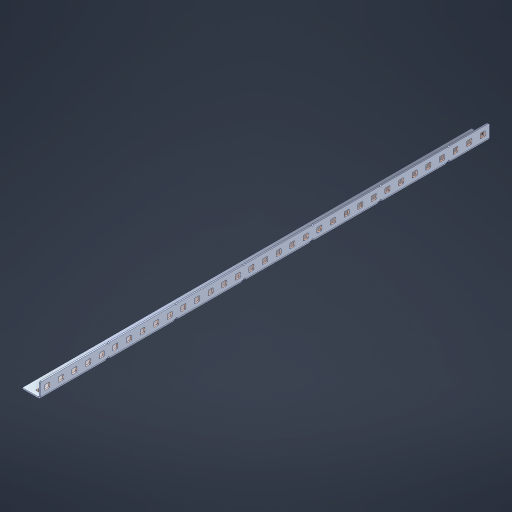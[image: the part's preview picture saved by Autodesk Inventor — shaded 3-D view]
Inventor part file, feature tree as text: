
AUTODESK INVENTOR PART (.ipt)
format: ipt  version: 2023 (Build 270158000, 158)  size: 1,009,152 bytes
history: native  units: in
note: dims shown in document units (in); Inventor stores cm internally (conversion verified against a paired STEP export)
features: other x71, extrude x65, sheet_metal_op x10, sketch x8, mirror x1, pattern_linear x1, chamfer x1
ambient origin geometry x8: Origin, YZ Plane, XZ Plane, XY Plane, X Axis, Y Axis, Z Axis, Center Point
bodies: Solid1 (feature_tree), Body (feature_tree)
feature tree (157):
  other  "Flange Pattern Plane"
  sheet_metal_op  "Flange Pattern"
  sheet_metal_op  "Body Pattern"
  other  "Arc Length"
  mirror  "Notch Mirror"
  pattern_linear  "Notch Pattern"  Spacing1=0.1875in  [1 undecoded]
  chamfer  "End Chamfer"
  extrude  "Half Cut"  Depth=0.0469in
  sketch  "Sketch1"  dims[d0=2.5in]
  other  "Plate1"
  sketch  "Sketch2"  dims[d1=16.5in]
  other  "Plate2"
  sheet_metal_op  "Bend1"
  sheet_metal_op  "Corner1"
  sketch  "Sketch3"  dims[d2=0.0469in]
  other  "Flange Pattern Sketch"
  sketch  "Sketch7"  dims[d3=0.0469in]
  other  "Srf1"
  other  "Srf2"
  sketch  "Sketch8"  dims[d4=0.0234in]
  sketch  "Sketch9"  dims[d5=0.0938in]
  other  "Srf91"
  sheet_metal_op  "Body Pattern Sketch"
  other  "Srf92"
  sketch  "Sketch13"  dims[d6=0.0469in]
  sketch  "Sketch14"  dims[d7=0.5in d8=90.0deg d9=0.0312in d10=0.1875in d11=0.0469in d12=0.0469in d16=0.182in d17=0.02in d18=0.0469in d19=0.0in d20=0.25in d21=0.25in d46=0.172in d47=1.0in d48=0.0in d49=0.182in d50=0.02in d51=0.25in d52=0.25in d53=0.0469in d54=0.0in d55=0.172in d56=1.0in d57=0.0in d60=12.9921in d62=0.5in d63=0.3937in d65=0.5in d85=0.1227in d86=0.1659in d88=0.04in d89=0.0469in d90=0.0in d91=0.04in d92=0.0491in d95=2.5in d96=0.04in d97=0.25in d98=45.0deg d101=0.0in d102=2.497in d131=0.5in d132=12.9921in d134=0.5in d139=0.5in]
  other  "Srf856"
  other  "Srf1310"
  other  "Srf1311"
  other  "Srf1312"
  other  "Srf1376"
  other  "Srf1377"
  other  "Srf1728"
  other  "Srf1755"
  other  "Srf1878"
  other  "Srf1879"
  other  "Srf1880"
  other  "Srf1881"
  other  "Srf1882"
  other  "Srf1883"
  other  "Srf1884"
  other  "Srf1885"
  other  "Srf1886"
  other  "Srf1887"
  other  "Srf1888"
  other  "Srf1889"
  other  "Srf1890"
  other  "Srf1891"
  other  "Srf1892"
  other  "Srf1893"
  other  "Srf1894"
  other  "Srf1895"
  other  "Srf1896"
  other  "Srf1897"
  other  "Srf1898"
  other  "Srf1899"
  other  "Srf1900"
  other  "Srf1901"
  other  "Srf1902"
  other  "Srf1903"
  other  "Srf1904"
  other  "Srf1942"
  other  "Srf1943"
  other  "Srf1944"
  other  "Srf1945"
  other  "Srf1946"
  other  "Srf1947"
  other  "Srf1948"
  other  "Srf1949"
  other  "Srf1950"
  other  "Srf1951"
  other  "Srf1952"
  other  "Srf1953"
  other  "Srf1954"
  other  "Srf1955"
  other  "Srf1956"
  other  "Srf1957"
  other  "Srf1958"
  other  "Srf1959"
  other  "Srf1960"
  other  "Srf1961"
  other  "Srf1962"
  other  "Srf1963"
  other  "Srf1964"
  other  "Srf1965"
  other  "Srf1966"
  other  "Srf1967"
  other  "Srf1968"
  sheet_metal_op  "Flange Stamp"
  sheet_metal_op  "Flange Circle"
  sheet_metal_op  "Body Stamp"
  sheet_metal_op  "Body Circle"
  sheet_metal_op  "Notch"
  extrude  "ExtrusionSrf2"  Depth=0.0469in
  extrude  "ExtrusionSrf92"  Depth=0.5in
  extrude  "ExtrusionSrf856"  Depth=0.02in
  extrude  "ExtrusionSrf1310"  Depth=0.0469in
  extrude  "ExtrusionSrf1311"  TaperAngle=0.0deg  [1 undecoded]
  extrude  "ExtrusionSrf1312"  Depth=0.5in
  extrude  "ExtrusionSrf1376"  Depth=0.5in
  extrude  "ExtrusionSrf1377"  Depth=0.5in
  extrude  "ExtrusionSrf1728"  Depth=0.5in TaperAngle=0.0deg
  extrude  "ExtrusionSrf1755"  Depth=0.5in
  extrude  "ExtrusionSrf1878"  Depth=0.02in
  extrude  "ExtrusionSrf1879"  Depth=0.5in
  extrude  "ExtrusionSrf1880"  Depth=0.5in
  extrude  "ExtrusionSrf1881"  Depth=0.0469in
  extrude  "ExtrusionSrf1882"  TaperAngle=0.0deg  [1 undecoded]
  extrude  "ExtrusionSrf1883"  Depth=0.5in
  extrude  "ExtrusionSrf1884"  Depth=0.5in TaperAngle=0.0deg
  extrude  "ExtrusionSrf1885"  Depth=0.5in
  extrude  "ExtrusionSrf1886"  Depth=0.5in
  extrude  "ExtrusionSrf1887"  Depth=0.5in
  extrude  "ExtrusionSrf1888"  Depth=0.5in
  extrude  "ExtrusionSrf1889"  Depth=0.5in
  extrude  "ExtrusionSrf1890"  Depth=0.0469in
  extrude  "ExtrusionSrf1891"  TaperAngle=0.0deg  [1 undecoded]
  extrude  "ExtrusionSrf1892"  Depth=0.5in
  extrude  "ExtrusionSrf1893"  Depth=0.5in
  extrude  "ExtrusionSrf1894"  Depth=0.5in
  extrude  "ExtrusionSrf1895"  Depth=0.5in TaperAngle=45.0deg
  extrude  "ExtrusionSrf1896"  TaperAngle=0.0deg  [1 undecoded]
  extrude  "ExtrusionSrf1897"  Depth=0.5in
  extrude  "ExtrusionSrf1898"  Depth=0.5in
  extrude  "ExtrusionSrf1899"  Depth=0.5in
  extrude  "ExtrusionSrf1900"  Depth=0.5in
  extrude  "ExtrusionSrf1901"  Depth=0.5in
  extrude  "ExtrusionSrf1902"  [1 undecoded]
  extrude  "ExtrusionSrf1903"  [1 undecoded]
  extrude  "ExtrusionSrf1904"  [1 undecoded]
  extrude  "ExtrusionSrf1942"  [1 undecoded]
  extrude  "ExtrusionSrf1943"  [1 undecoded]
  extrude  "ExtrusionSrf1944"  [1 undecoded]
  extrude  "ExtrusionSrf1945"  [1 undecoded]
  extrude  "ExtrusionSrf1946"  [1 undecoded]
  extrude  "ExtrusionSrf1947"  [1 undecoded]
  extrude  "ExtrusionSrf1948"  [1 undecoded]
  extrude  "ExtrusionSrf1949"  [1 undecoded]
  extrude  "ExtrusionSrf1950"  [1 undecoded]
  extrude  "ExtrusionSrf1951"  [1 undecoded]
  extrude  "ExtrusionSrf1952"  [1 undecoded]
  extrude  "ExtrusionSrf1953"  [1 undecoded]
  extrude  "ExtrusionSrf1954"  [1 undecoded]
  extrude  "ExtrusionSrf1955"  [1 undecoded]
  extrude  "ExtrusionSrf1956"  [1 undecoded]
  extrude  "ExtrusionSrf1957"  [1 undecoded]
  extrude  "ExtrusionSrf1958"  [1 undecoded]
  extrude  "ExtrusionSrf1959"  [1 undecoded]
  extrude  "ExtrusionSrf1960"  [1 undecoded]
  extrude  "ExtrusionSrf1961"  [1 undecoded]
  extrude  "ExtrusionSrf1962"  [1 undecoded]
  extrude  "ExtrusionSrf1963"  [1 undecoded]
  extrude  "ExtrusionSrf1964"  [1 undecoded]
  extrude  "ExtrusionSrf1965"  [1 undecoded]
  extrude  "ExtrusionSrf1966"  [1 undecoded]
  extrude  "ExtrusionSrf1967"  [1 undecoded]
  extrude  "ExtrusionSrf1968"  [1 undecoded]
note: 35 required parameter values undecoded (feature->parameter linkage not recoverable at this tier; creation-order binding heuristic only, values carry confidence <= 0.55)
